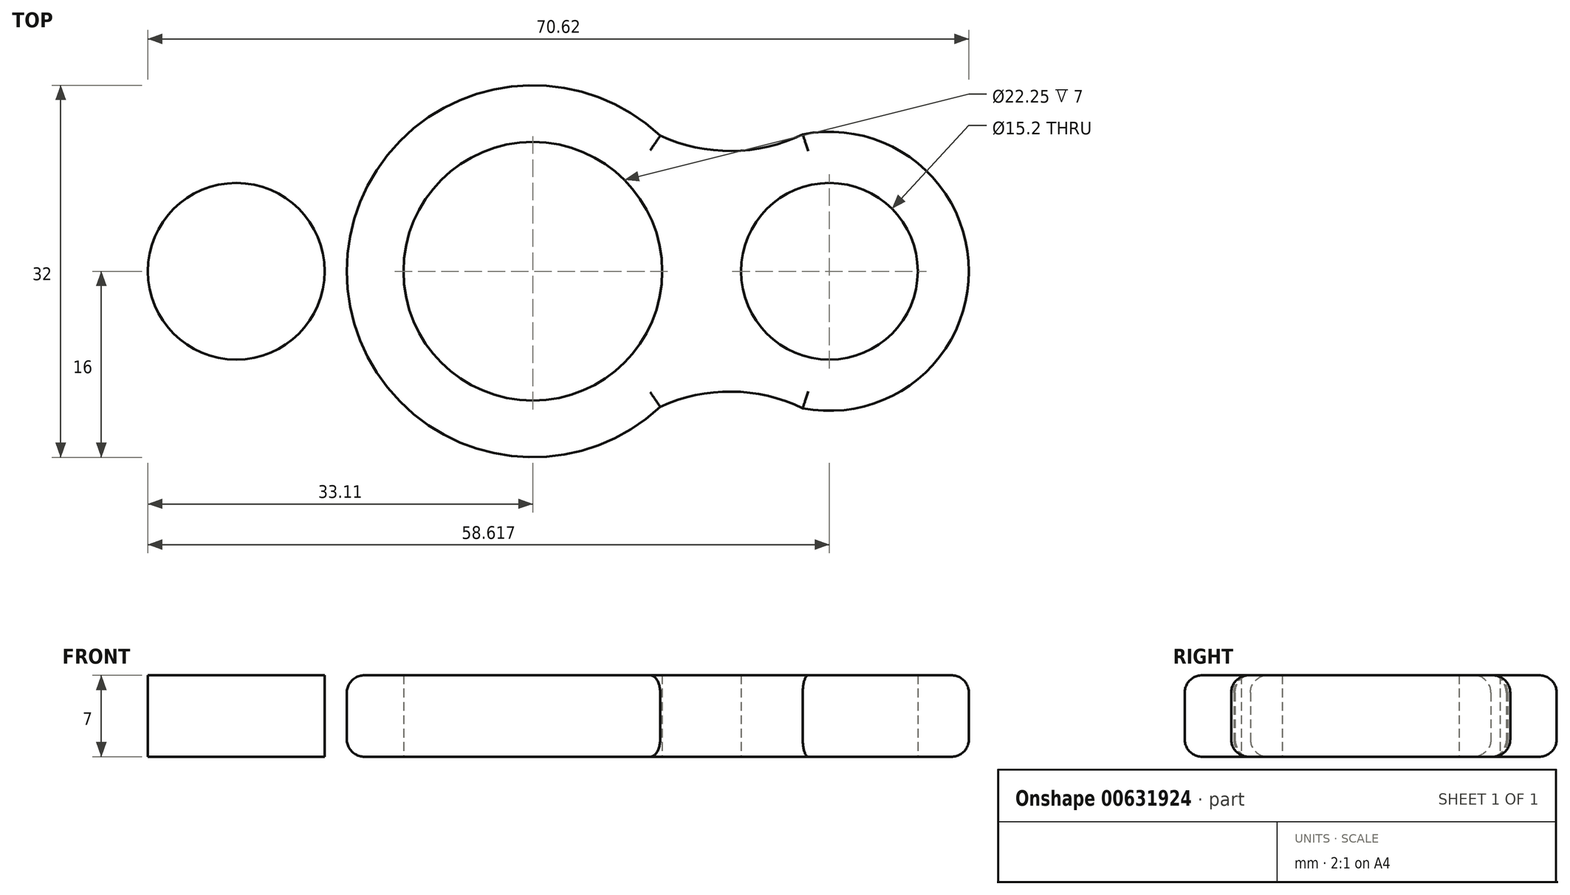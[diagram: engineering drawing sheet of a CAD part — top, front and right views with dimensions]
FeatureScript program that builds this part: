
annotation { "Feature Type Name" : "Feature", "Feature Type Description" : "" }
export const myFeature = defineFeature(function(context is Context, id is Id, definition is map)
    precondition{}
    {
        {
            var Q0;
            Q0=qCreatedBy(makeId("Top.planeOp"),FACE);
            var sketch = newSketch(context, id + "F0", { "sketchPlane" : qUnion([Q0])});
            skCircle(sketch, "E0", {"center": v(0, 0) * mm, "radius": 11.12 * mm});
            skCircle(sketch, "E1", {"center": v(0, 0) * mm, "radius": 16 * mm});
            skLineSegment(sketch, "E2", {"start": v(0, 0) * mm, "end": v(34.83, 0) * mm, "construction": true});
            skCircle(sketch, "E3", {"center": v(25.5, 0) * mm, "radius": 7.6 * mm});
            skArc(sketch, "E4", {"start": v(20.04, -10.68) * mm, "mid": v(37.5, 0) * mm, "end": v(20.04, 10.68) * mm});
            skArc(sketch, "E5", {"start": v(23.21, -11.78) * mm, "mid": v(17.1, -10.35) * mm, "end": v(10.96, -11.66) * mm});
            skArc(sketch, "E6.MirrorCS", {"start": v(23.21, 11.78) * mm, "mid": v(17.1, 10.35) * mm, "end": v(10.96, 11.66) * mm});
            skLineSegment(sketch, "E7.MirrorCS", {"start": v(0, 0) * mm, "end": v(-34.83, 0) * mm, "construction": true});
            skCircle(sketch, "E8.MirrorC", {"center": v(-25.5, 0) * mm, "radius": 7.6 * mm});
            skArc(sketch, "E9.MirrorC", {"start": v(-20.04, -10.68) * mm, "mid": v(-37.5, 0) * mm, "end": v(-20.04, 10.68) * mm});
            skArc(sketch, "E10.MirrorCS", {"start": v(-23.21, -11.78) * mm, "mid": v(-17.1, -10.35) * mm, "end": v(-10.96, -11.66) * mm});
            skArc(sketch, "E11.MirrorCS", {"start": v(-23.21, 11.78) * mm, "mid": v(-17.1, 10.35) * mm, "end": v(-10.96, 11.66) * mm});
            skSolve(sketch);
        }
        {
            var Q0;
            Q0=makeQuery(id+"F0.imprint","IMPRINT",FACE,{"disambiguationData":[TD([[makeQuery(id+"F0.imprint","IMPRINT",EDGE,{"derivedFrom":sQuery(id+"F0.wireOp",EDGE,"E8.MirrorC")}),1.0]])]});
            var Q1;
            Q1=makeQuery(id+"F0.imprint","IMPRINT",FACE,{"disambiguationData":[TD([[makeQuery(id+"F0.imprint","IMPRINT",EDGE,{"derivedFrom":sQuery(id+"F0.wireOp",EDGE,"E0")}),-1.0]])]});
            var Q2;
            Q2=makeQuery(id+"F0.imprint","IMPRINT",FACE,{"disambiguationData":[TD([[makeQuery(id+"F0.imprint","IMPRINT",EDGE,{"derivedFrom":sQuery(id+"F0.wireOp",EDGE,"E3")}),-1.0]])]});
            extrude(context, id + "F1", {"entities" : qUnion([Q0, Q1, Q2]), "depth" : 7 * mm, "offsetDistance" : 25 * mm});
        }
        {
            var Q0;
            Q0=makeQuery(id+"F1.opExtrude","CAP_EDGE",EDGE,{"disambiguationData":[OSD([sQuery(id+"F0.wireOp",EDGE,"E9.MirrorC")])],"isStart":false});
            var Q1;
            Q1=makeQuery(id+"F1.opExtrude","CAP_EDGE",EDGE,{"disambiguationData":[OSD([sQuery(id+"F0.wireOp",EDGE,"E11.MirrorCS")])],"isStart":false});
            var Q2;
            Q2=makeQuery(id+"F1.opExtrude","CAP_EDGE",EDGE,{"disambiguationData":[OSD([sQuery(id+"F0.wireOp",EDGE,"E10.MirrorCS")])],"isStart":false});
            var Q3;
            {var subQ0=sQuery(id+"F0.wireOp",EDGE,"E1");Q3=makeQuery(id+"F1.opExtrude","CAP_EDGE",EDGE,{"disambiguationData":[OSD([subQ0]),TDD([makeQuery(id+"F0.imprint","IMPRINT",EDGE,{"disambiguationData":[TD([[makeQuery(id+"F0.imprint","INTERSECT",VERTEX,{"derivedFrom":[subQ0,sQuery(id+"F0.wireOp",EDGE,"E5")]}),1.0]])],"derivedFrom":subQ0})])],"isStart":false});}
            var Q4;
            Q4=makeQuery(id+"F1.opExtrude","CAP_EDGE",EDGE,{"disambiguationData":[OSD([sQuery(id+"F0.wireOp",EDGE,"E5")])],"isStart":false});
            var Q5;
            Q5=makeQuery(id+"F1.opExtrude","CAP_EDGE",EDGE,{"disambiguationData":[OSD([sQuery(id+"F0.wireOp",EDGE,"E4")])],"isStart":false});
            var Q6;
            Q6=makeQuery(id+"F1.opExtrude","CAP_EDGE",EDGE,{"disambiguationData":[OSD([sQuery(id+"F0.wireOp",EDGE,"E6.MirrorCS")])],"isStart":false});
            var Q7;
            {var subQ0=sQuery(id+"F0.wireOp",EDGE,"E1");Q7=makeQuery(id+"F1.opExtrude","CAP_EDGE",EDGE,{"disambiguationData":[OSD([subQ0]),TDD([makeQuery(id+"F0.imprint","IMPRINT",EDGE,{"disambiguationData":[TD([[makeQuery(id+"F0.imprint","INTERSECT",VERTEX,{"derivedFrom":[subQ0,sQuery(id+"F0.wireOp",EDGE,"E6.MirrorCS")]}),-1.0]])],"derivedFrom":subQ0})])],"isStart":false});}
            var Q8;
            {var subQ0=sQuery(id+"F0.wireOp",EDGE,"E1");Q8=makeQuery(id+"F1.opExtrude","CAP_EDGE",EDGE,{"disambiguationData":[OSD([subQ0]),TDD([makeQuery(id+"F0.imprint","IMPRINT",EDGE,{"disambiguationData":[TD([[makeQuery(id+"F0.imprint","INTERSECT",VERTEX,{"derivedFrom":[subQ0,sQuery(id+"F0.wireOp",EDGE,"E5")]}),1.0]])],"derivedFrom":subQ0})])],"isStart":true});}
            var Q9;
            Q9=makeQuery(id+"F1.opExtrude","CAP_EDGE",EDGE,{"disambiguationData":[OSD([sQuery(id+"F0.wireOp",EDGE,"E5")])],"isStart":true});
            var Q10;
            Q10=makeQuery(id+"F1.opExtrude","CAP_EDGE",EDGE,{"disambiguationData":[OSD([sQuery(id+"F0.wireOp",EDGE,"E4")])],"isStart":true});
            var Q11;
            Q11=makeQuery(id+"F1.opExtrude","CAP_EDGE",EDGE,{"disambiguationData":[OSD([sQuery(id+"F0.wireOp",EDGE,"E6.MirrorCS")])],"isStart":true});
            var Q12;
            {var subQ0=sQuery(id+"F0.wireOp",EDGE,"E1");Q12=makeQuery(id+"F1.opExtrude","CAP_EDGE",EDGE,{"disambiguationData":[OSD([subQ0]),TDD([makeQuery(id+"F0.imprint","IMPRINT",EDGE,{"disambiguationData":[TD([[makeQuery(id+"F0.imprint","INTERSECT",VERTEX,{"derivedFrom":[subQ0,sQuery(id+"F0.wireOp",EDGE,"E6.MirrorCS")]}),-1.0]])],"derivedFrom":subQ0})])],"isStart":true});}
            var Q13;
            Q13=makeQuery(id+"F1.opExtrude","CAP_EDGE",EDGE,{"disambiguationData":[OSD([sQuery(id+"F0.wireOp",EDGE,"E11.MirrorCS")])],"isStart":true});
            var Q14;
            Q14=makeQuery(id+"F1.opExtrude","CAP_EDGE",EDGE,{"disambiguationData":[OSD([sQuery(id+"F0.wireOp",EDGE,"E9.MirrorC")])],"isStart":true});
            var Q15;
            Q15=makeQuery(id+"F1.opExtrude","CAP_EDGE",EDGE,{"disambiguationData":[OSD([sQuery(id+"F0.wireOp",EDGE,"E10.MirrorCS")])],"isStart":true});
            fillet(context, id + "F2", {"entities" : qUnion([Q0, Q1, Q2, Q3, Q4, Q5, Q6, Q7, Q8, Q9, Q10, Q11, Q12, Q13, Q14, Q15]), "radius" : 1.5 * mm, "tangentPropagation" : true, "allowEdgeOverflow" : false});
        }
    });
